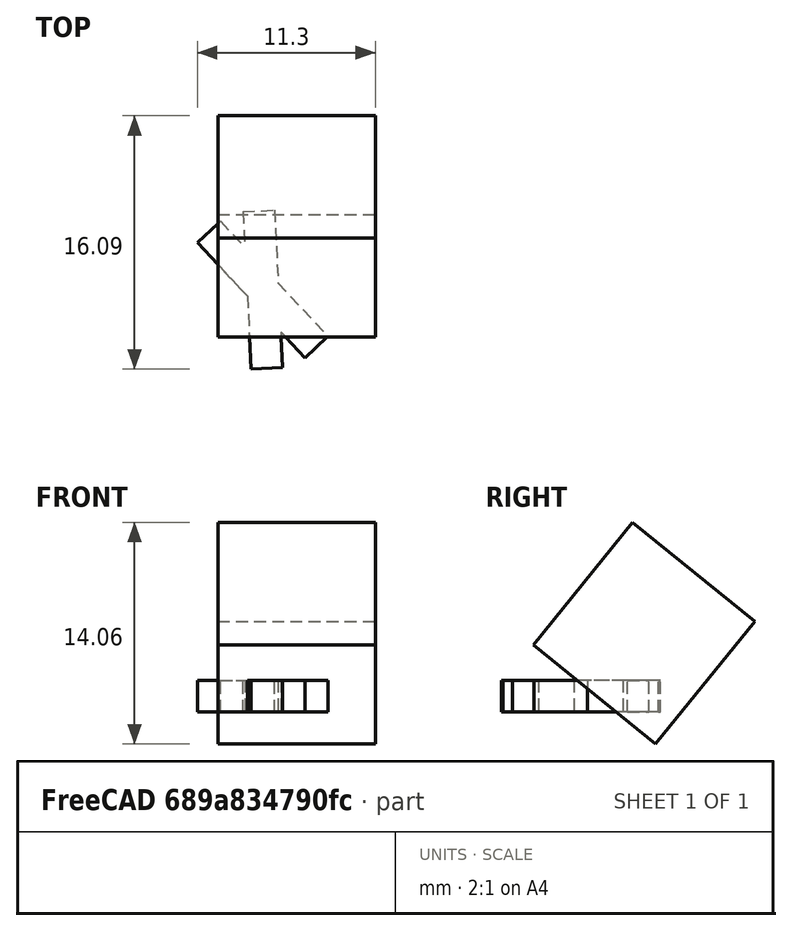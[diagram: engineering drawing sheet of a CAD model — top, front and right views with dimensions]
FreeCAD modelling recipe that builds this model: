
FCSTD DOCUMENT  (FreeCAD 1.0R39285 (Git))
Label: ojt1_t06p01_rotations
License: All rights reserved
objects: Part::Box×3, Part::MultiFuse×1
note: 4 computed .brp shape members not serialized (recipe doc carries the construction recipe); baked Part::Feature solids carry a one-line shape summary decoded from their .brp

FEATURE [Part::Box] Box  label="Cub"
  AttacherType = Attacher::AttachEngine3D
  Height = 10
  Length = 10
  Placement = pos=(4,10.7391,-2.03233) rot=(1,0,0;0.890118rad)
  Width = 10
FEATURE [Part::Box] Box001  label="Cub001"
  AttacherType = Attacher::AttachEngine3D
  Height = 2
  Length = 10
  Placement = pos=(8.56167,10.7889,0) rot=(0,0,1;4.17134rad)
  Width = 2
FEATURE [Part::Box] Box002  label="Cub002"
  AttacherType = Attacher::AttachEngine3D
  Height = 2
  Length = 10
  Placement = pos=(11.2457,8.55668,-1e-16) rot=(0,0,-1;2.80998rad)
  Width = 2
FEATURE [Part::MultiFuse] Fusion
  Placement = pos=(10.7122,-2.24289,0) rot=(0,0,1;1.29154rad)
  Refine = true
  Shapes = -> [Box001,Box002]
